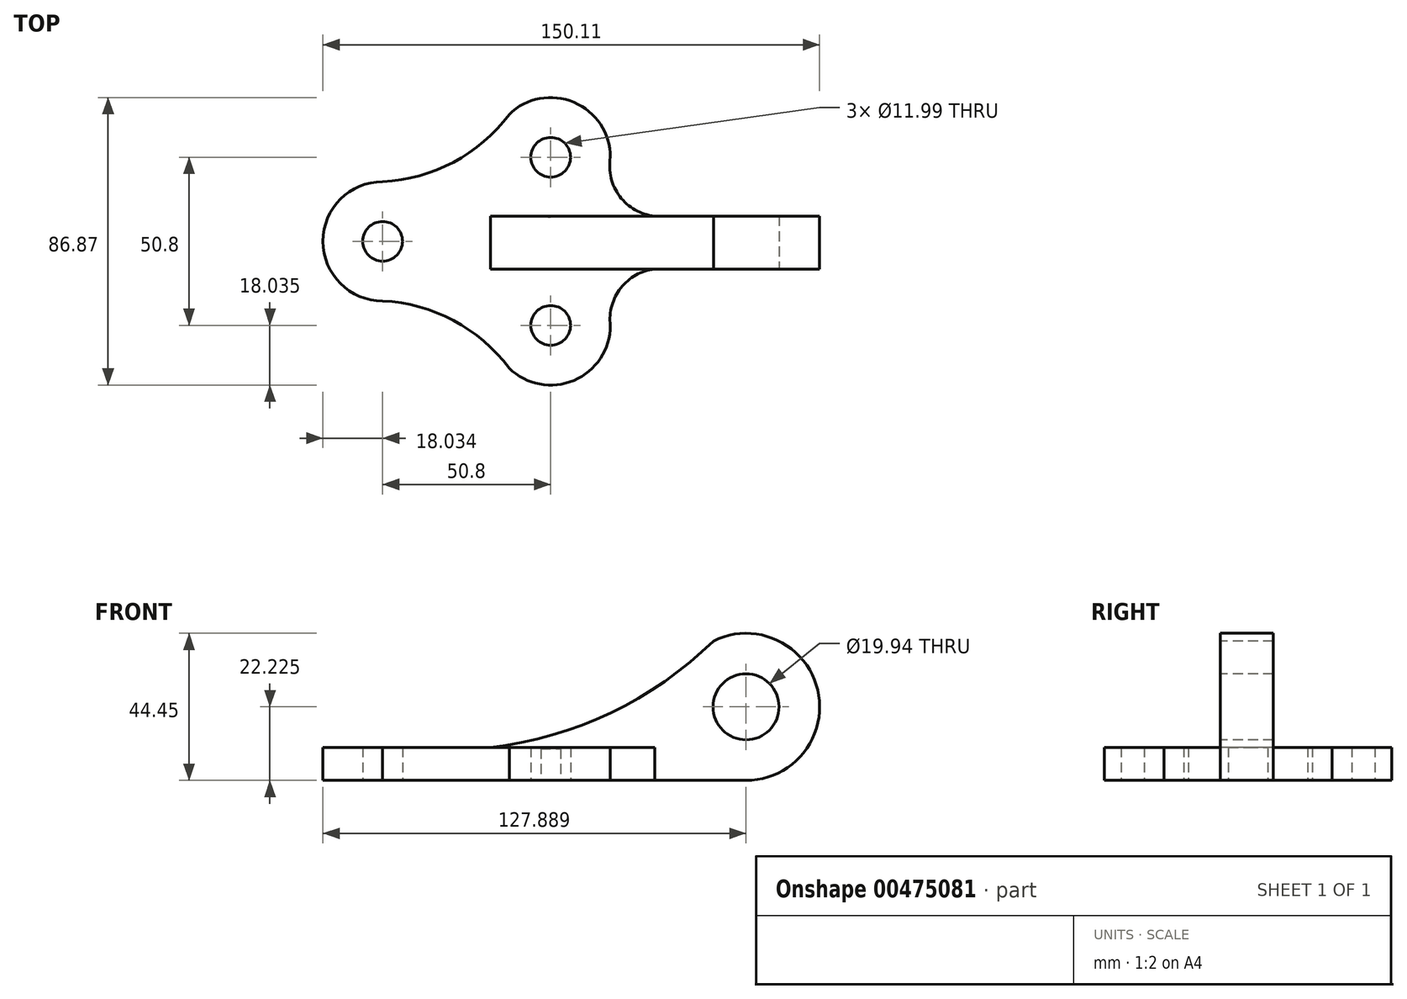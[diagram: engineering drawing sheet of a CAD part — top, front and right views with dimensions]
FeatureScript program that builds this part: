
annotation { "Feature Type Name" : "Feature", "Feature Type Description" : "" }
export const myFeature = defineFeature(function(context is Context, id is Id, definition is map)
    precondition{}
    {
        {
            var Q0;
            Q0=qCreatedBy(makeId("Top.planeOp"),FACE);
            var sketch = newSketch(context, id + "F0", { "sketchPlane" : qUnion([Q0])});
            skCircle(sketch, "E0", {"center": v(28.42, 37.25) * mm, "radius": 6 * mm});
            skCircle(sketch, "E1", {"center": v(28.42, -13.55) * mm, "radius": 6 * mm});
            skCircle(sketch, "E2", {"center": v(-22.38, 11.85) * mm, "radius": 6 * mm});
            skCircle(sketch, "E3", {"center": v(-22.38, 11.85) * mm, "radius": 18.03 * mm});
            skCircle(sketch, "E4", {"center": v(28.42, -13.55) * mm, "radius": 18.03 * mm});
            skCircle(sketch, "E5", {"center": v(28.42, 37.25) * mm, "radius": 18.03 * mm});
            skArc(sketch, "E6", {"start": v(15.88, -26.5) * mm, "mid": v(-0.98, -12.07) * mm, "end": v(-22.38, -6.19) * mm});
            skArc(sketch, "E7", {"start": v(-22.38, 29.88) * mm, "mid": v(-0.98, 35.76) * mm, "end": v(15.88, 50.2) * mm});
            skLineSegment(sketch, "E8.bottom", {"start": v(-22.38, 19.46) * mm, "end": v(87.48, 19.46) * mm});
            skLineSegment(sketch, "E8.top", {"start": v(-22.38, 3.46) * mm, "end": v(87.48, 3.46) * mm});
            skLineSegment(sketch, "E8.left", {"start": v(-22.38, 19.46) * mm, "end": v(-22.38, 3.46) * mm});
            skLineSegment(sketch, "E8.right", {"start": v(87.48, 19.46) * mm, "end": v(87.48, 3.46) * mm});
            skArc(sketch, "E9", {"start": v(46.46, 37.25) * mm, "mid": v(49.29, 25.45) * mm, "end": v(59.84, 19.46) * mm});
            skArc(sketch, "E10", {"start": v(59.84, 3.46) * mm, "mid": v(49.6, -2.26) * mm, "end": v(46.46, -13.55) * mm});
            skLineSegment(sketch, "E11", {"start": v(59.84, 3.46) * mm, "end": v(59.84, 19.46) * mm});
            skSolve(sketch);
        }
        {
            var Q0;
            {var subQ0=sQuery(id+"F0.wireOp",EDGE,"E8.top");var subQ1=sQuery(id+"F0.wireOp",EDGE,"E4");var subQ2=makeQuery(id+"F0.imprint","INTERSECT",VERTEX,{"disambiguationData":[OD(0.0)],"derivedFrom":[subQ1,subQ0]});Q0=makeQuery(id+"F0.imprint","IMPRINT",FACE,{"disambiguationData":[TD([[makeQuery(id+"F0.imprint","IMPRINT",EDGE,{"disambiguationData":[TD([[subQ2,-1.0]])],"derivedFrom":subQ1}),1.0]])]});}
            var Q1;
            {var subQ0=sQuery(id+"F0.wireOp",EDGE,"E8.bottom");var subQ1=sQuery(id+"F0.wireOp",EDGE,"E5");var subQ2=makeQuery(id+"F0.imprint","INTERSECT",VERTEX,{"disambiguationData":[OD(0.0)],"derivedFrom":[subQ1,subQ0]});Q1=makeQuery(id+"F0.imprint","IMPRINT",FACE,{"disambiguationData":[TD([[makeQuery(id+"F0.imprint","IMPRINT",EDGE,{"disambiguationData":[TD([[subQ2,-1.0]])],"derivedFrom":subQ1}),1.0]])]});}
            var Q2;
            {var subQ7=sQuery(id+"F0.wireOp",EDGE,"E8.left");var subQ8=sQuery(id+"F0.wireOp",EDGE,"E2");var subQ9=makeQuery(id+"F0.imprint","INTERSECT",VERTEX,{"disambiguationData":[OD(0.0)],"derivedFrom":[subQ8,subQ7]});Q2=makeQuery(id+"F0.imprint","IMPRINT",FACE,{"disambiguationData":[TD([[makeQuery(id+"F0.imprint","IMPRINT",EDGE,{"disambiguationData":[TD([[subQ9,-1.0]])],"derivedFrom":subQ8}),-1.0]])]});}
            var Q3;
            {var subQ0=sQuery(id+"F0.wireOp",EDGE,"E7");var subQ1=sQuery(id+"F0.wireOp",EDGE,"E3");var subQ2=makeQuery(id+"F0.imprint","INTERSECT",VERTEX,{"derivedFrom":[subQ1,subQ0]});Q3=makeQuery(id+"F0.imprint","IMPRINT",FACE,{"disambiguationData":[TD([[makeQuery(id+"F0.imprint","IMPRINT",EDGE,{"disambiguationData":[TD([[subQ2,1.0]])],"derivedFrom":subQ1}),-1.0]])]});}
            var Q4;
            Q4=makeQuery(id+"F0.imprint","IMPRINT",FACE,{"disambiguationData":[TD([[makeQuery(id+"F0.imprint","IMPRINT",EDGE,{"derivedFrom":sQuery(id+"F0.wireOp",EDGE,"E0")}),-1.0]])]});
            var Q5;
            {var subQ0=sQuery(id+"F0.wireOp",EDGE,"E9");var subQ1=sQuery(id+"F0.wireOp",EDGE,"E5");var subQ2=makeQuery(id+"F0.imprint","INTERSECT",VERTEX,{"disambiguationData":[OD(1.0)],"derivedFrom":[subQ1,subQ0]});Q5=makeQuery(id+"F0.imprint","IMPRINT",FACE,{"disambiguationData":[TD([[makeQuery(id+"F0.imprint","IMPRINT",EDGE,{"disambiguationData":[TD([[subQ2,1.0]])],"derivedFrom":subQ1}),-1.0]])]});}
            var Q6;
            {var subQ0=sQuery(id+"F0.wireOp",EDGE,"E6");var subQ1=sQuery(id+"F0.wireOp",EDGE,"E3");var subQ2=makeQuery(id+"F0.imprint","INTERSECT",VERTEX,{"derivedFrom":[subQ1,subQ0]});Q6=makeQuery(id+"F0.imprint","IMPRINT",FACE,{"disambiguationData":[TD([[makeQuery(id+"F0.imprint","IMPRINT",EDGE,{"disambiguationData":[TD([[subQ2,-1.0]])],"derivedFrom":subQ1}),-1.0]])]});}
            var Q7;
            {var subQ9=sQuery(id+"F0.wireOp",EDGE,"E11");Q7=makeQuery(id+"F0.imprint","IMPRINT",FACE,{"disambiguationData":[TD([[makeQuery(id+"F0.imprint","IMPRINT",EDGE,{"derivedFrom":subQ9}),1.0]])]});}
            var Q8;
            {var subQ0=sQuery(id+"F0.wireOp",EDGE,"E10");var subQ1=sQuery(id+"F0.wireOp",EDGE,"E4");var subQ2=makeQuery(id+"F0.imprint","INTERSECT",VERTEX,{"disambiguationData":[OD(1.0)],"derivedFrom":[subQ1,subQ0]});Q8=makeQuery(id+"F0.imprint","IMPRINT",FACE,{"disambiguationData":[TD([[makeQuery(id+"F0.imprint","IMPRINT",EDGE,{"disambiguationData":[TD([[subQ2,-1.0]])],"derivedFrom":subQ1}),-1.0]])]});}
            var Q9;
            {var subQ0=sQuery(id+"F0.wireOp",EDGE,"E8.left");var subQ8=sQuery(id+"F0.wireOp",EDGE,"E2");var subQ9=makeQuery(id+"F0.imprint","INTERSECT",VERTEX,{"disambiguationData":[OD(0.0)],"derivedFrom":[subQ8,subQ0]});Q9=makeQuery(id+"F0.imprint","IMPRINT",FACE,{"disambiguationData":[TD([[makeQuery(id+"F0.imprint","IMPRINT",EDGE,{"disambiguationData":[TD([[subQ9,1.0]])],"derivedFrom":subQ8}),-1.0]])]});}
            var Q10;
            Q10=makeQuery(id+"F0.imprint","IMPRINT",FACE,{"disambiguationData":[TD([[makeQuery(id+"F0.imprint","IMPRINT",EDGE,{"derivedFrom":sQuery(id+"F0.wireOp",EDGE,"E1")}),-1.0]])]});
            extrude(context, id + "F1", {"entities" : qUnion([Q0, Q1, Q2, Q3, Q4, Q5, Q6, Q7, Q8, Q9, Q10]), "depth" : 10 * mm});
        }
        {
            var Q0;
            {var subQ0=sQuery(id+"F0.wireOp",EDGE,"E8.right");Q0=makeQuery(id+"F0.imprint","IMPRINT",FACE,{"disambiguationData":[TD([[makeQuery(id+"F0.imprint","IMPRINT",EDGE,{"derivedFrom":subQ0}),-1.0]])]});}
            extrude(context, id + "F2", {"entities" : qUnion([Q0]), "operationType" : NewBodyOperationType.ADD, "depth" : 2.54 * mm});
        }
        {
            var Q0;
            Q0=makeQuery(id+"F2.opExtrude","SWEPT_FACE",FACE,{"disambiguationData":[OSD([sQuery(id+"F0.wireOp",EDGE,"E8.top")])]});
            var sketch = newSketch(context, id + "F3", { "sketchPlane" : qUnion([Q0])});
            skArc(sketch, "E12", {"start": v(68.87, 34.37) * mm, "mid": v(102.24, 5.6) * mm, "end": v(77.6, 42.14) * mm});
            skCircle(sketch, "E13", {"center": v(87.48, 22.23) * mm, "radius": 9.97 * mm});
            skArc(sketch, "E14", {"start": v(-10.74, 9.59) * mm, "mid": v(36.94, 16.34) * mm, "end": v(77.6, 42.14) * mm});
            skLineSegment(sketch, "E15", {"start": v(-10.74, 9.59) * mm, "end": v(59.78, 9.59) * mm});
            skLineSegment(sketch, "E16", {"start": v(59.78, 9.59) * mm, "end": v(59.84, 2.54) * mm});
            skLineSegment(sketch, "E17", {"start": v(59.84, 2.54) * mm, "end": v(77.16, 2.54) * mm});
            skSolve(sketch);
        }
        {
            var Q0;
            Q0 = qSketchRegion(id + "F3", true);
            extrude(context, id + "F4", {"entities" : qUnion([Q0]), "operationType" : NewBodyOperationType.ADD, "oppositeDirection" : true, "depth" : 16 * mm});
        }
    });
